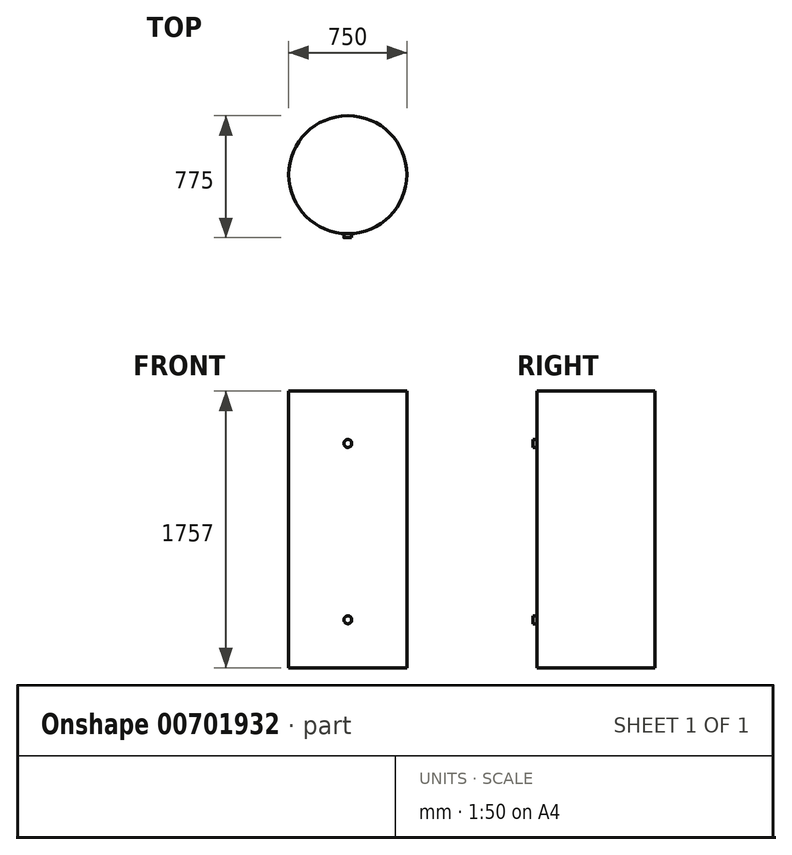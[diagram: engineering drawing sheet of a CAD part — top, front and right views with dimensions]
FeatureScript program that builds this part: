
annotation { "Feature Type Name" : "Feature", "Feature Type Description" : "" }
export const myFeature = defineFeature(function(context is Context, id is Id, definition is map)
    precondition{}
    {
        {
            var Q0;
            Q0=qCreatedBy(makeId("Top.planeOp"),FACE);
            var sketch = newSketch(context, id + "F0", { "sketchPlane" : qUnion([Q0])});
            skCircle(sketch, "E0", {"center": v(0, 0) * mm, "radius": 375 * mm});
            skSolve(sketch);
        }
        {
            var Q0;
            Q0=makeQuery(id+"F0.imprint","IMPRINT",FACE,{"disambiguationData":[TD([[makeQuery(id+"F0.imprint","IMPRINT",EDGE,{"derivedFrom":sQuery(id+"F0.wireOp",EDGE,"E0")}),1.0]])]});
            extrude(context, id + "F1", {"entities" : qUnion([Q0]), "depth" : 1757 * mm, "offsetDistance" : 25 * mm});
        }
        {
            var Q0;
            Q0=qCreatedBy(makeId("Front.planeOp"),FACE);
            var sketch = newSketch(context, id + "F2", { "sketchPlane" : qUnion([Q0])});
            skCircle(sketch, "E1", {"center": v(0, 305) * mm, "radius": 25 * mm});
            skCircle(sketch, "E2", {"center": v(0, 1425) * mm, "radius": 25 * mm});
            skSolve(sketch);
        }
        {
            var Q0;
            Q0 = qSketchRegion(id + "F2", true);
            extrude(context, id + "F3", {"entities" : qUnion([Q0]), "operationType" : NewBodyOperationType.ADD, "depth" : 400 * mm, "offsetDistance" : 25 * mm});
        }
    });
